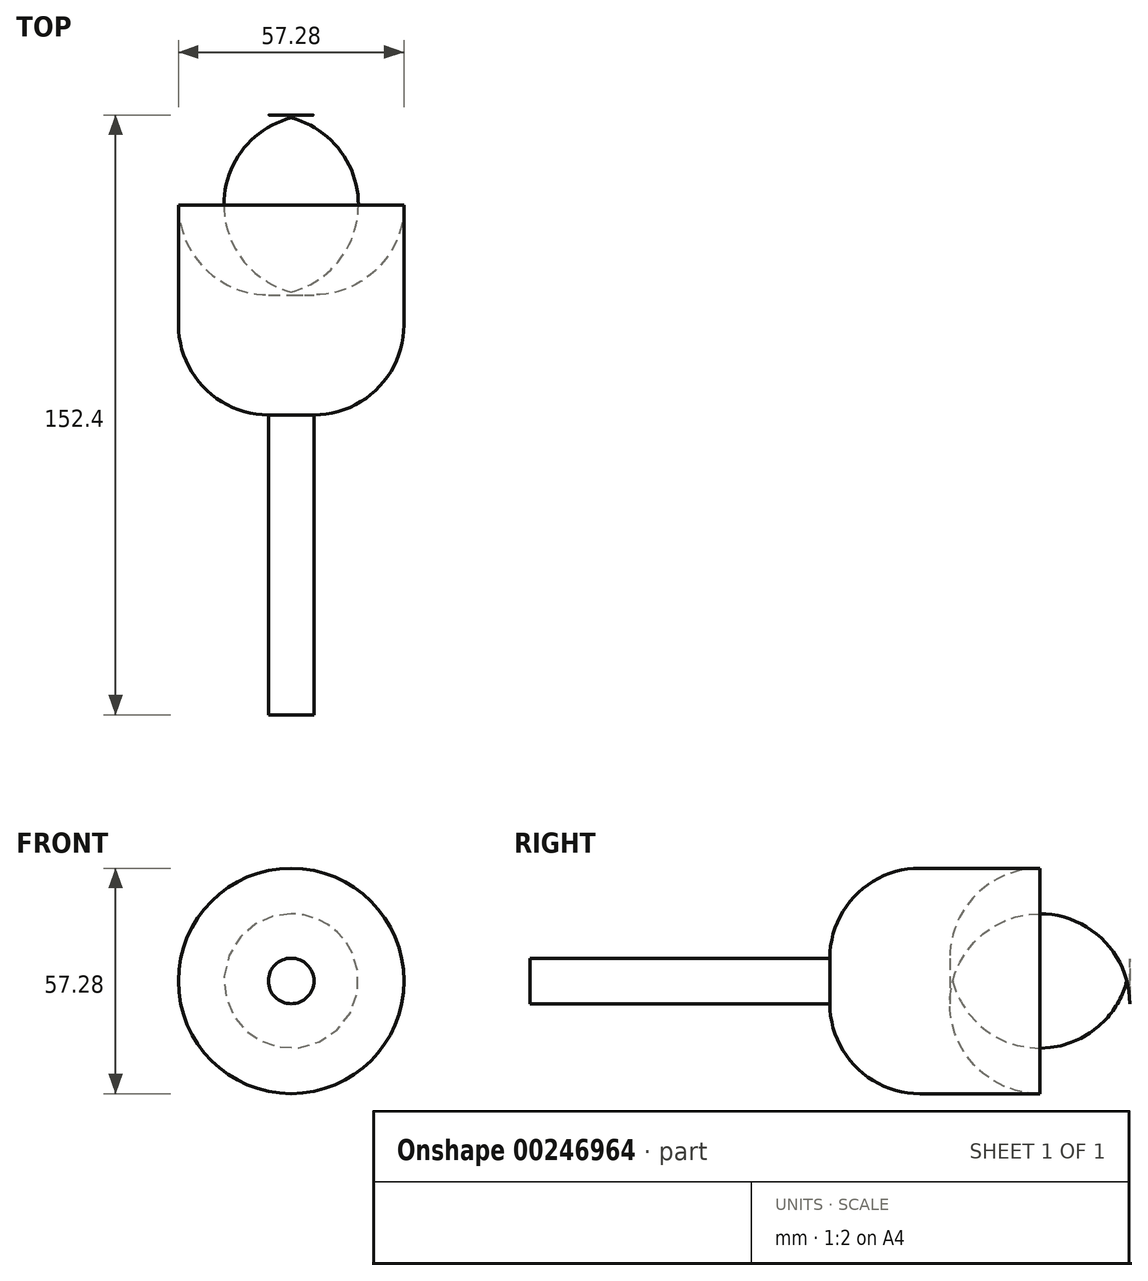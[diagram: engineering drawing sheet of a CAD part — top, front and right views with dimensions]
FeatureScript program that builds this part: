
annotation { "Feature Type Name" : "Feature", "Feature Type Description" : "" }
export const myFeature = defineFeature(function(context is Context, id is Id, definition is map)
    precondition{}
    {
        {
            var Q0;
            Q0=qCreatedBy(makeId("Front.planeOp"),FACE);
            var sketch = newSketch(context, id + "F0", { "sketchPlane" : qUnion([Q0])});
            skCircle(sketch, "E0", {"center": v(0, 0) * mm, "radius": 28.64 * mm});
            skSolve(sketch);
        }
        {
            var Q0;
            Q0 = qSketchRegion(id + "F0", true);
            extrude(context, id + "F1", {"entities" : qUnion([Q0]), "depth" : 76.2 * mm});
        }
        {
            var Q0;
            Q0=makeQuery(id+"F1.opExtrude","CAP_EDGE",EDGE,{"disambiguationData":[OSD([sQuery(id+"F0.wireOp",EDGE,"E0")])],"isStart":false});
            var Q1;
            Q1=makeQuery(id+"F1.opExtrude","SWEPT_FACE",FACE,{"disambiguationData":[OSD([sQuery(id+"F0.wireOp",EDGE,"E0")])]});
            fillet(context, id + "F2", {"entities" : qUnion([Q0, Q1]), "radius" : 22.86 * mm, "tangentPropagation" : true, "allowEdgeOverflow" : false});
        }
        {
            var Q0;
            Q0=makeQuery(id+"F1.opExtrude","CAP_FACE",FACE,{"disambiguationData":[OSD([sQuery(id+"F0.wireOp",EDGE,"E0")])],"isStart":true});
            extrude(context, id + "F3", {"entities" : qUnion([Q0]), "operationType" : NewBodyOperationType.ADD, "oppositeDirection" : true, "depth" : 152.4 * mm});
        }
    });
